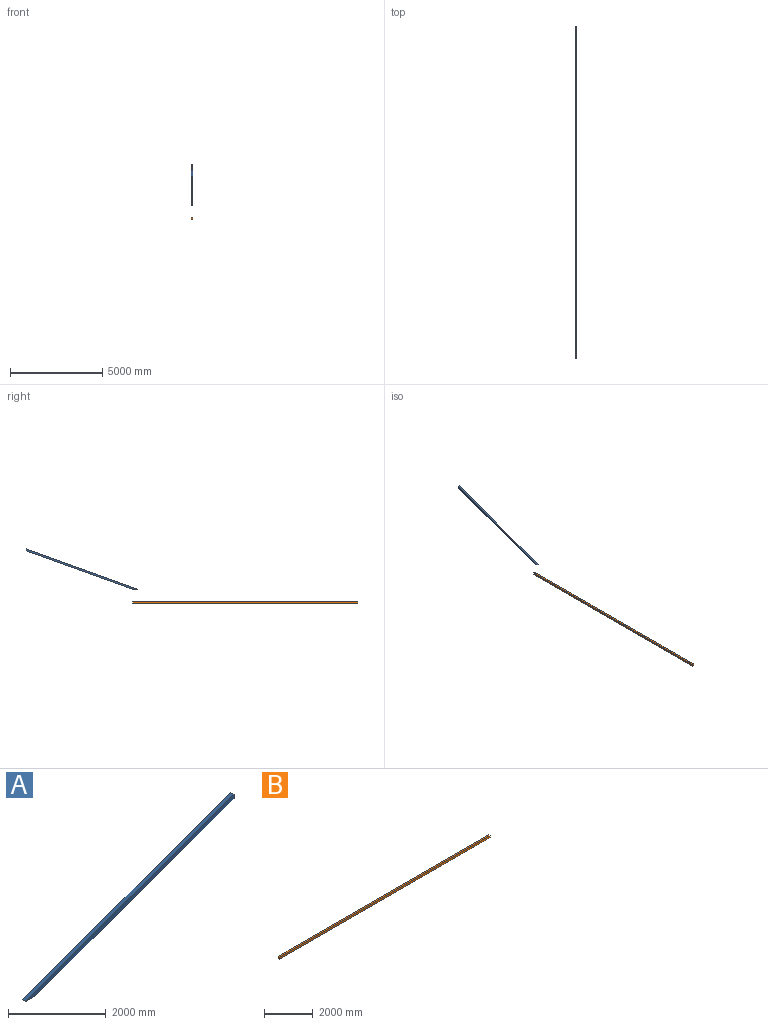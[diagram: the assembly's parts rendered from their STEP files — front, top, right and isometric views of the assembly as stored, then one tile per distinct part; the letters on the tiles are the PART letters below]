
ASSEMBLY  parts=2 mates=2
PART A: 6 faces, bbox 6050x100x2182 mm
  f0: plane 6050x2181.97mm, normal (-0.34,0,0.94), area 643144.5mm2, adj f1,f3,f4,f5
  f1: plane 294.75x100mm, normal (0,0,-1), area 29475.4mm2, adj f0,f2,f4,f5
  f2: plane 5755.25x2075.66mm, normal (0.34,0,-0.94), area 611810.6mm2, adj f1,f3,f4,f5
  f3: plane 106.31x100mm, normal (1,0,0), area 10630.5mm2, adj f0,f2,f4,f5
  f4: plane 6050x2181.97mm, normal (0,-1,0), area 627477.6mm2, adj f0,f1,f2,f3
  f5: plane 6050x2181.97mm, normal (0,1,0), area 627477.6mm2, adj f0,f1,f2,f3
PART B: 6 faces, bbox 12200x100x100 mm
  f0: plane 12200x100mm, normal (0,0,1), area 1220000mm2, adj f1,f3,f4,f5
  f1: plane 100x100mm, normal (-1,0,0), area 10000mm2, adj f0,f2,f4,f5
  f2: plane 12200x100mm, normal (0,0,-1), area 1220000mm2, adj f1,f3,f4,f5
  f3: plane 100x100mm, normal (1,0,0), area 10000mm2, adj f0,f2,f4,f5
  f4: plane 12200x100mm, normal (0,-1,0), area 1220000mm2, adj f0,f1,f2,f3
  f5: plane 12200x100mm, normal (0,1,0), area 1220000mm2, adj f0,f1,f2,f3
PLACE A rot(axis=(0,0,1),90deg) t=(-103.71,5848.48,809.38)mm
PLACE B rot(axis=(0.71,-0.71,0),180deg) t=(-103.71,6105.86,59.38)mm
MATE parallel B.f0 <-> A.f1  axis (0,0,-1) through (-53.71,5.86,59.38)mm
MATE planar B.f4 <-> A.f4  axis (1,0,0) through (-3.71,5.86,109.38)mm
